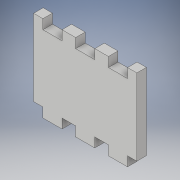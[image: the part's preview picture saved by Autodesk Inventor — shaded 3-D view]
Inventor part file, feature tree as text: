
AUTODESK INVENTOR PART (.ipt)
format: ipt  version: 2018 (Build 220112000, 112)  size: 141,312 bytes
history: native  units: in
note: dims shown in document units (in); Inventor stores cm internally (conversion verified against a paired STEP export)
features: extrude x3, sketch x3
ambient origin geometry x8: Origin, YZ Plane, XZ Plane, XY Plane, X Axis, Y Axis, Z Axis, Center Point
bodies: Solid1 (feature_tree)
feature tree (6):
  extrude  "Extrusion1"  Depth=2.0in
  extrude  "Extrusion2"  Depth=0.25in TaperAngle=0.0deg
  extrude  "Extrusion3"  Depth=1.55in
  sketch  "Sketch1"  dims[d0=2.7in d1=2.0in]
  sketch  "Sketch2"  dims[d9=0.25in d10=0.0in d12=0.25in d13=0.0in]
  sketch  "Sketch3"  dims[d15=2.37in d16=1.55in d17=0.15in d18=0.0in]
